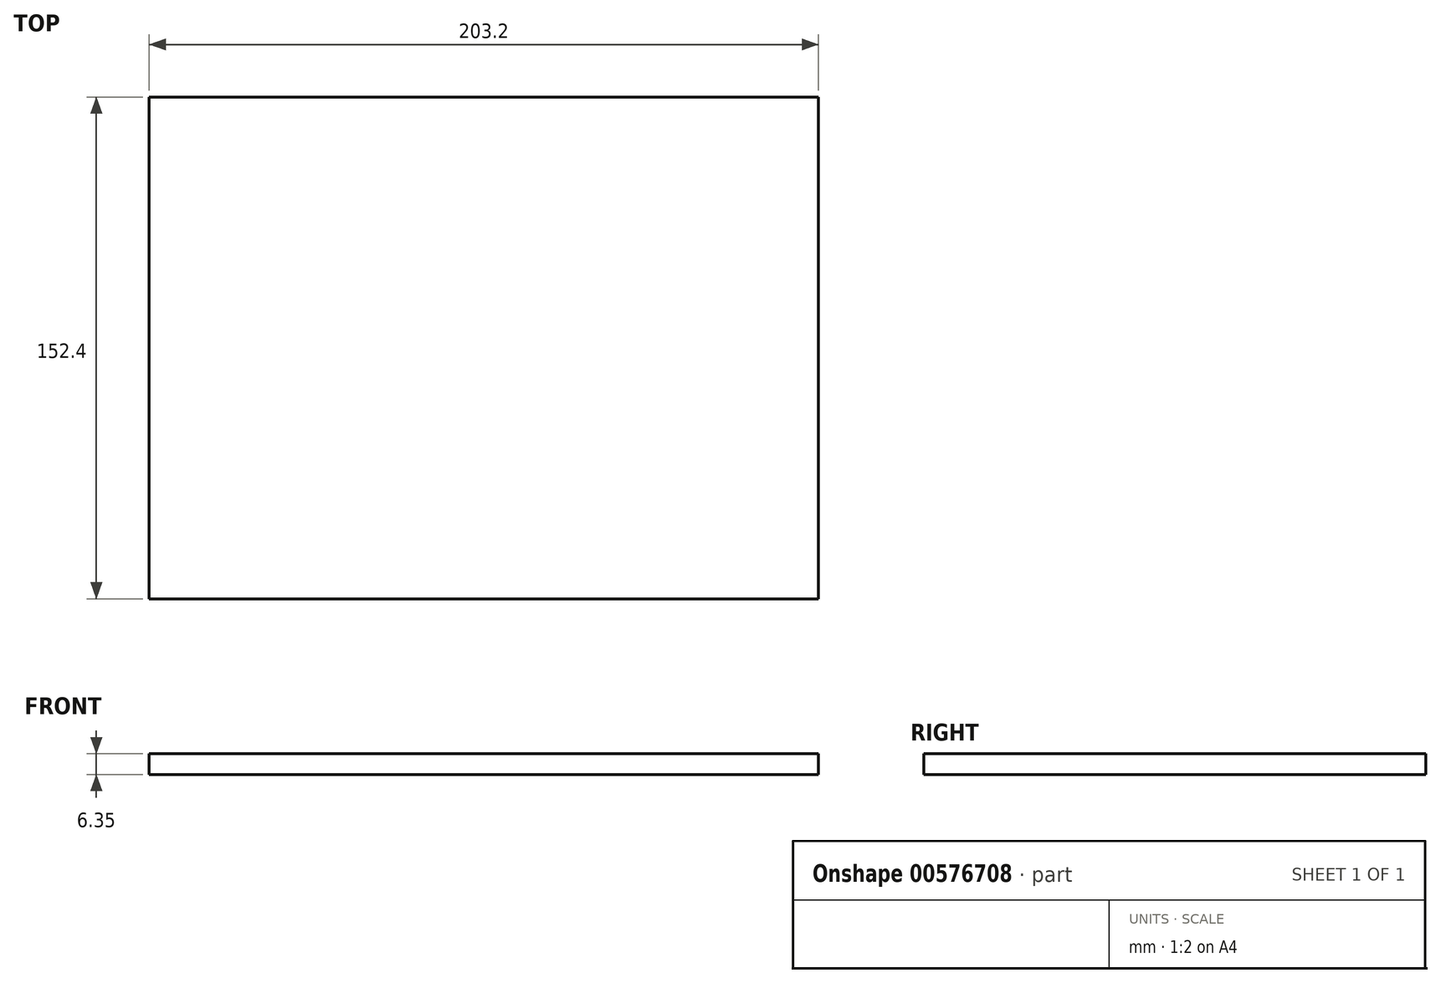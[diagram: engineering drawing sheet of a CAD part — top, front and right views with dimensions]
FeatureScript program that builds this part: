
annotation { "Feature Type Name" : "Feature", "Feature Type Description" : "" }
export const myFeature = defineFeature(function(context is Context, id is Id, definition is map)
    precondition{}
    {
        {
            var Q0;
            Q0=qCreatedBy(makeId("Top.planeOp"),FACE);
            var sketch = newSketch(context, id + "F0", { "sketchPlane" : qUnion([Q0])});
            skLineSegment(sketch, "E0.bottom", {"start": v(101.6, 76.2) * mm, "end": v(-101.6, 76.2) * mm});
            skLineSegment(sketch, "E0.top", {"start": v(101.6, -76.2) * mm, "end": v(-101.6, -76.2) * mm});
            skLineSegment(sketch, "E0.left", {"start": v(101.6, 76.2) * mm, "end": v(101.6, -76.2) * mm});
            skLineSegment(sketch, "E0.right", {"start": v(-101.6, 76.2) * mm, "end": v(-101.6, -76.2) * mm});
            skPoint(sketch, "E0.middle", {"position": v(0, 0) * mm});
            skSolve(sketch);
        }
        {
            var Q0;
            Q0 = qSketchRegion(id + "F0", true);
            extrude(context, id + "F1", {"entities" : qUnion([Q0]), "depth" : 6.35 * mm, "offsetDistance" : 25.4 * mm});
        }
    });
